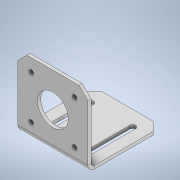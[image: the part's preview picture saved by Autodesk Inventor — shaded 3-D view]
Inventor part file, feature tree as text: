
AUTODESK INVENTOR PART (.ipt)
format: ipt  version: 2022 (Build 260153000, 153)  size: 163,328 bytes
history: native  units: in
note: dims shown in document units (in); Inventor stores cm internally (conversion verified against a paired STEP export)
features: sheet_metal_op x2, hole x2, other x2, sketch x1
ambient origin geometry x8: Origin, YZ Plane, XZ Plane, XY Plane, X Axis, Y Axis, Z Axis, Center Point
bodies: Solid1 (feature_tree)
feature tree (7):
  sketch  "Sketch1"  dims[d0=1.9685in d1=3.937in d2=1.1811in d3=0.0827in d4=0.4331in d5=1.1811in d6=1.9291in d7=1.2205in d8=1.2205in d9=0.09in d10=0.09in d11=0.045in d12=0.18in d13=0.09in d14=90.0deg d15=0.09in d16=0.1339in d17=0.75in d18=0.256in d19=0.118in d20=90.0deg d21=0.09in d22=0.8108in d23=0.8661in d24=0.75in d25=0.375in d26=0.25in d27=0.5635in d28=1.0in d29=0.8108in d30=0.25in d31=0.25in d32=45.0deg]
  sheet_metal_op  "Face1"
  sheet_metal_op  "Fold1"
  hole  "Hole1"  [1 undecoded]
  hole  "Hole2"  [1 undecoded]
  other  "Corner Chamfer1"
  other  "Plate1"
note: 2 required parameter values undecoded (feature->parameter linkage not recoverable at this tier; creation-order binding heuristic only, values carry confidence <= 0.55)
